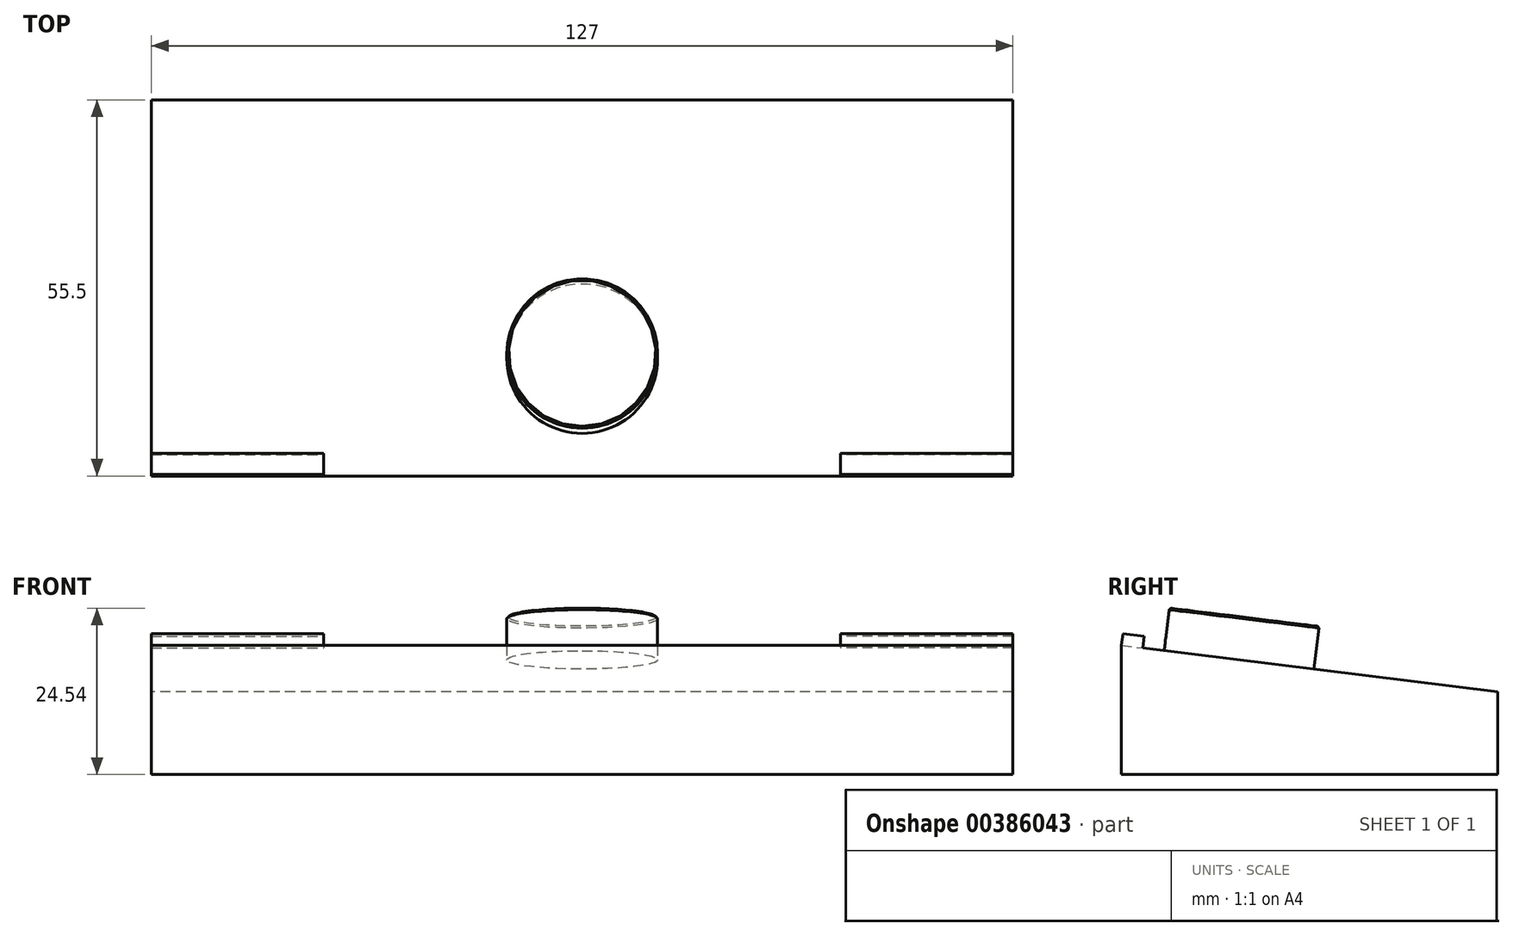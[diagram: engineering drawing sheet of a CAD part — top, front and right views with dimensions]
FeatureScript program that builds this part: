
annotation { "Feature Type Name" : "Feature", "Feature Type Description" : "" }
export const myFeature = defineFeature(function(context is Context, id is Id, definition is map)
    precondition{}
    {
        {
            var Q0;
            Q0=qCreatedBy(makeId("Right.planeOp"),FACE);
            var sketch = newSketch(context, id + "F0", { "sketchPlane" : qUnion([Q0])});
            skCircle(sketch, "E0", {"center": v(0, 0) * mm, "radius": 3.18 * mm});
            skLineSegment(sketch, "E1", {"start": v(-3.18, 0) * mm, "end": v(-3.18, 25.19) * mm});
            skLineSegment(sketch, "E2", {"start": v(51.9, -3.17) * mm, "end": v(-3.18, 3.59) * mm});
            skLineSegment(sketch, "E3", {"start": v(-3.18, 3.59) * mm, "end": v(-0.85, 22.5) * mm});
            skLineSegment(sketch, "E4", {"start": v(-0.85, 22.5) * mm, "end": v(54.23, 15.73) * mm});
            skLineSegment(sketch, "E5", {"start": v(54.23, 15.73) * mm, "end": v(51.9, -3.17) * mm});
            skLineSegment(sketch, "E6", {"start": v(0, -3.18) * mm, "end": v(59.55, -3.18) * mm});
            skLineSegment(sketch, "E7", {"start": v(54.23, 15.73) * mm, "end": v(54.23, -3.17) * mm});
            skCircle(sketch, "E8", {"center": v(53.14, -2.08) * mm, "radius": 1.1 * mm});
            skPoint(sketch, "E8.first.point", {"position": v(52.05, -1.95) * mm});
            skPoint(sketch, "E8.second.point", {"position": v(53.14, -3.17) * mm});
            skPoint(sketch, "E8.third.point", {"position": v(54.23, -2.08) * mm});
            skLineSegment(sketch, "E9", {"start": v(-3.18, 3.59) * mm, "end": v(52.74, 3.59) * mm});
            skLineSegment(sketch, "E10", {"start": v(0, 36.89) * mm, "end": v(-55.5, 36.89) * mm});
            skLineSegment(sketch, "E11", {"start": v(-55.5, 36.89) * mm, "end": v(-55.5, 55.94) * mm});
            skLineSegment(sketch, "E12", {"start": v(-55.5, 55.94) * mm, "end": v(0, 49.12) * mm});
            skLineSegment(sketch, "E13", {"start": v(0, 49.12) * mm, "end": v(0, 36.89) * mm});
            skSolve(sketch);
        }
        {
            var Q0;
            Q0=makeQuery(id+"F0.imprint","IMPRINT",FACE,{"disambiguationData":[TD([[makeQuery(id+"F0.imprint","IMPRINT",EDGE,{"derivedFrom":sQuery(id+"F0.wireOp",EDGE,"E10")}),-1.0]])]});
            extrude(context, id + "F1", {"entities" : qUnion([Q0]), "depth" : 127 * mm, "offsetDistance" : 25.4 * mm});
        }
        {
            var Q0;
            Q0=makeQuery(id+"F1.opExtrude","SWEPT_FACE",FACE,{"disambiguationData":[OSD([sQuery(id+"F0.wireOp",EDGE,"E12")])]});
            var sketch = newSketch(context, id + "F2", { "sketchPlane" : qUnion([Q0])});
            skCircle(sketch, "E14", {"center": v(63.5, -44.44) * mm, "radius": 11.11 * mm});
            skLineSegment(sketch, "E15.bottom", {"start": v(127, -61.9) * mm, "end": v(101.6, -61.9) * mm});
            skLineSegment(sketch, "E15.top", {"start": v(127, -58.73) * mm, "end": v(101.6, -58.73) * mm});
            skLineSegment(sketch, "E15.left", {"start": v(127, -61.9) * mm, "end": v(127, -58.73) * mm});
            skLineSegment(sketch, "E15.right", {"start": v(101.6, -61.9) * mm, "end": v(101.6, -58.73) * mm});
            skLineSegment(sketch, "E16.bottom", {"start": v(0, -61.9) * mm, "end": v(25.4, -61.9) * mm});
            skLineSegment(sketch, "E16.top", {"start": v(0, -58.73) * mm, "end": v(25.4, -58.73) * mm});
            skLineSegment(sketch, "E16.left", {"start": v(0, -61.9) * mm, "end": v(0, -58.73) * mm});
            skLineSegment(sketch, "E16.right", {"start": v(25.4, -61.9) * mm, "end": v(25.4, -58.73) * mm});
            skSolve(sketch);
        }
        {
            var Q0;
            Q0=makeQuery(id+"F2.imprint","IMPRINT",FACE,{"disambiguationData":[TD([[makeQuery(id+"F2.imprint","IMPRINT",EDGE,{"derivedFrom":sQuery(id+"F2.wireOp",EDGE,"E14")}),1.0]])]});
            extrude(context, id + "F3", {"entities" : qUnion([Q0]), "operationType" : NewBodyOperationType.ADD, "depth" : 6.35 * mm, "offsetDistance" : 25.4 * mm});
        }
        {
            var Q0;
            Q0=makeQuery(id+"F3.opExtrude","CAP_EDGE",EDGE,{"disambiguationData":[OSD([sQuery(id+"F2.wireOp",EDGE,"E14")])],"isStart":false});
            chamfer(context, id + "F4", {"entities" : qUnion([Q0]), "width" : 0.25 * mm, "tangentPropagation" : true});
        }
        {
            var Q0;
            Q0=makeQuery(id+"F2.imprint","IMPRINT",FACE,{"disambiguationData":[TD([[makeQuery(id+"F2.imprint","IMPRINT",EDGE,{"derivedFrom":sQuery(id+"F2.wireOp",EDGE,"E15.bottom")}),-1.0]])]});
            var Q1;
            Q1=makeQuery(id+"F2.imprint","IMPRINT",FACE,{"disambiguationData":[TD([[makeQuery(id+"F2.imprint","IMPRINT",EDGE,{"derivedFrom":sQuery(id+"F2.wireOp",EDGE,"E16.bottom")}),-1.0]])]});
            extrude(context, id + "F5", {"entities" : qUnion([Q0, Q1]), "operationType" : NewBodyOperationType.ADD, "depth" : 1.78 * mm, "offsetDistance" : 25.4 * mm});
        }
    });
